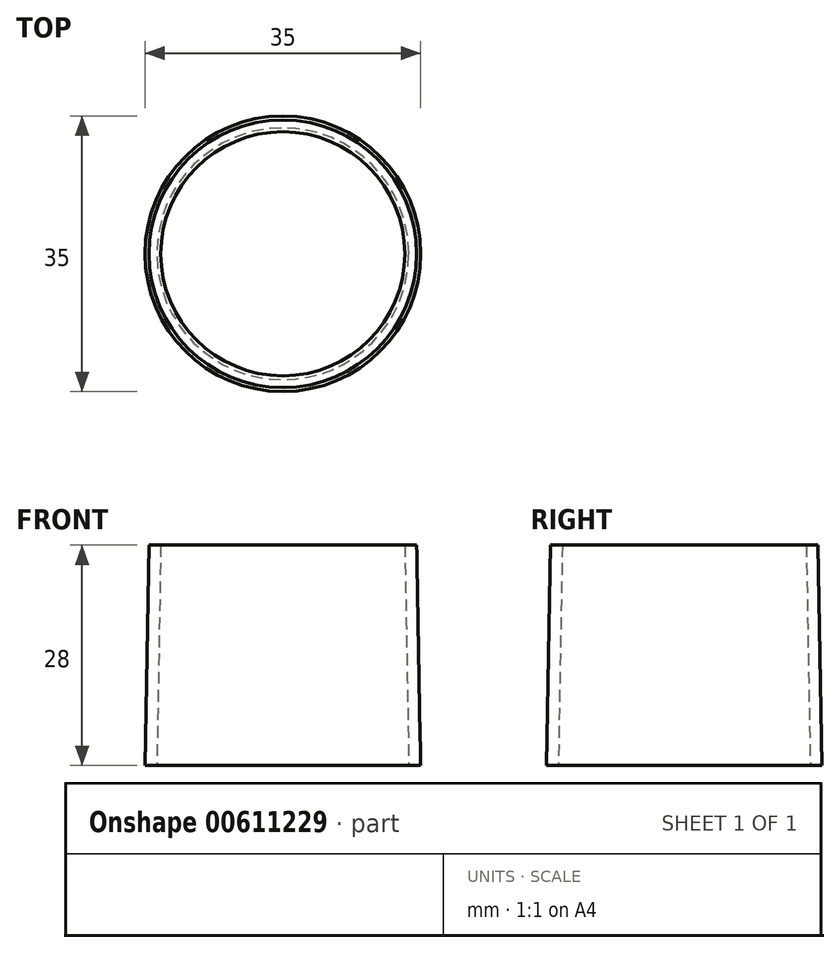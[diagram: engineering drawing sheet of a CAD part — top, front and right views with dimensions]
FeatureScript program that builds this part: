
annotation { "Feature Type Name" : "Feature", "Feature Type Description" : "" }
export const myFeature = defineFeature(function(context is Context, id is Id, definition is map)
    precondition{}
    {
        {
            var Q0;
            Q0=qCreatedBy(makeId("Front.planeOp"),FACE);
            var sketch = newSketch(context, id + "F0", { "sketchPlane" : qUnion([Q0])});
            skLineSegment(sketch, "E0", {"start": v(16, 0) * mm, "end": v(15.5, 28) * mm});
            skLineSegment(sketch, "E1", {"start": v(15.5, 28) * mm, "end": v(17, 28) * mm});
            skLineSegment(sketch, "E2", {"start": v(17, 28) * mm, "end": v(17.5, 0) * mm});
            skLineSegment(sketch, "E3", {"start": v(17.5, 0) * mm, "end": v(16, 0) * mm});
            skLineSegment(sketch, "E4", {"start": v(0, 55.24) * mm, "end": v(0, -38.2) * mm, "construction": true});
            skSolve(sketch);
        }
        {
            var Q0;
            Q0=makeQuery(id+"F0.imprint","IMPRINT",FACE,{"disambiguationData":[TD([[makeQuery(id+"F0.imprint","IMPRINT",EDGE,{"derivedFrom":sQuery(id+"F0.wireOp",EDGE,"E0")}),-1.0]])]});
            var Q1;
            Q1=sQuery(id+"F0.wireOp",EDGE,"E4");
            revolve(context, id + "F1", {"entities" : qUnion([Q0]), "axis" : qUnion([Q1]), "revolveType" : RevolveType.FULL});
        }
    });
